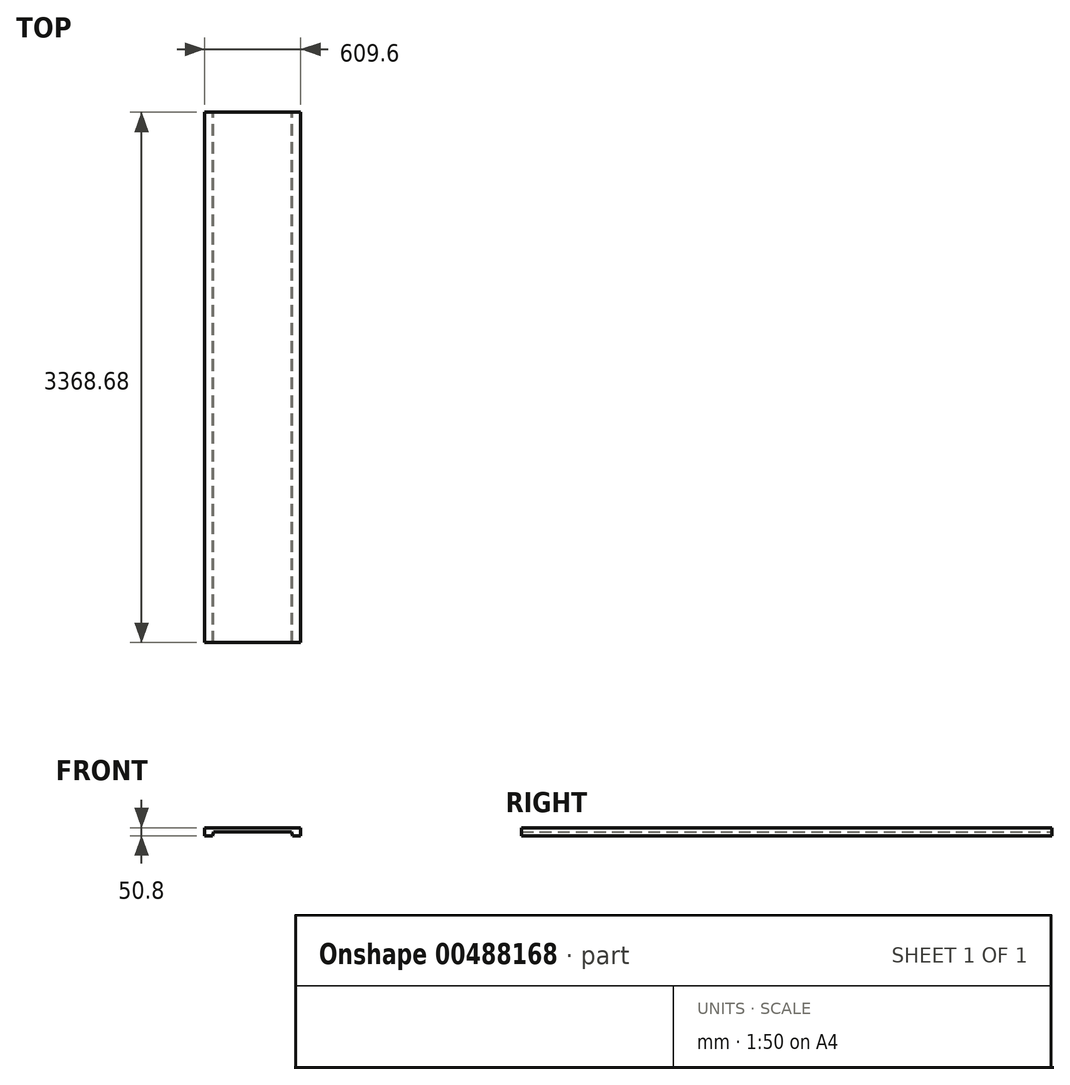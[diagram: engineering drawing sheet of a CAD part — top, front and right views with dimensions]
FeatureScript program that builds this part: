
annotation { "Feature Type Name" : "Feature", "Feature Type Description" : "" }
export const myFeature = defineFeature(function(context is Context, id is Id, definition is map)
    precondition{}
    {
        {
            var Q0;
            Q0=qCreatedBy(makeId("Front.planeOp"),FACE);
            var sketch = newSketch(context, id + "F0", { "sketchPlane" : qUnion([Q0])});
            skLineSegment(sketch, "E0", {"start": v(0, 0) * mm, "end": v(0, 50.8) * mm});
            skLineSegment(sketch, "E1", {"start": v(0, 50.8) * mm, "end": v(609.6, 50.8) * mm});
            skLineSegment(sketch, "E2", {"start": v(609.6, 50.8) * mm, "end": v(609.6, 0) * mm});
            skLineSegment(sketch, "E3", {"start": v(609.6, 0) * mm, "end": v(558.8, 0) * mm});
            skLineSegment(sketch, "E4", {"start": v(558.8, 0) * mm, "end": v(552, 25.4) * mm});
            skLineSegment(sketch, "E5", {"start": v(552, 25.4) * mm, "end": v(57.6, 25.4) * mm});
            skLineSegment(sketch, "E6", {"start": v(57.6, 25.4) * mm, "end": v(50.8, 0) * mm});
            skLineSegment(sketch, "E7", {"start": v(50.8, 0) * mm, "end": v(0, 0) * mm});
            skSolve(sketch);
        }
        {
            var Q0;
            Q0=makeQuery(id+"F0.imprint","IMPRINT",FACE,{"disambiguationData":[TD([[makeQuery(id+"F0.imprint","IMPRINT",EDGE,{"derivedFrom":sQuery(id+"F0.wireOp",EDGE,"E0")}),-1.0]])]});
            extrude(context, id + "F1", {"entities" : qUnion([Q0]), "depth" : 3368.67 * mm, "offsetDistance" : 25.4 * mm});
        }
    });
